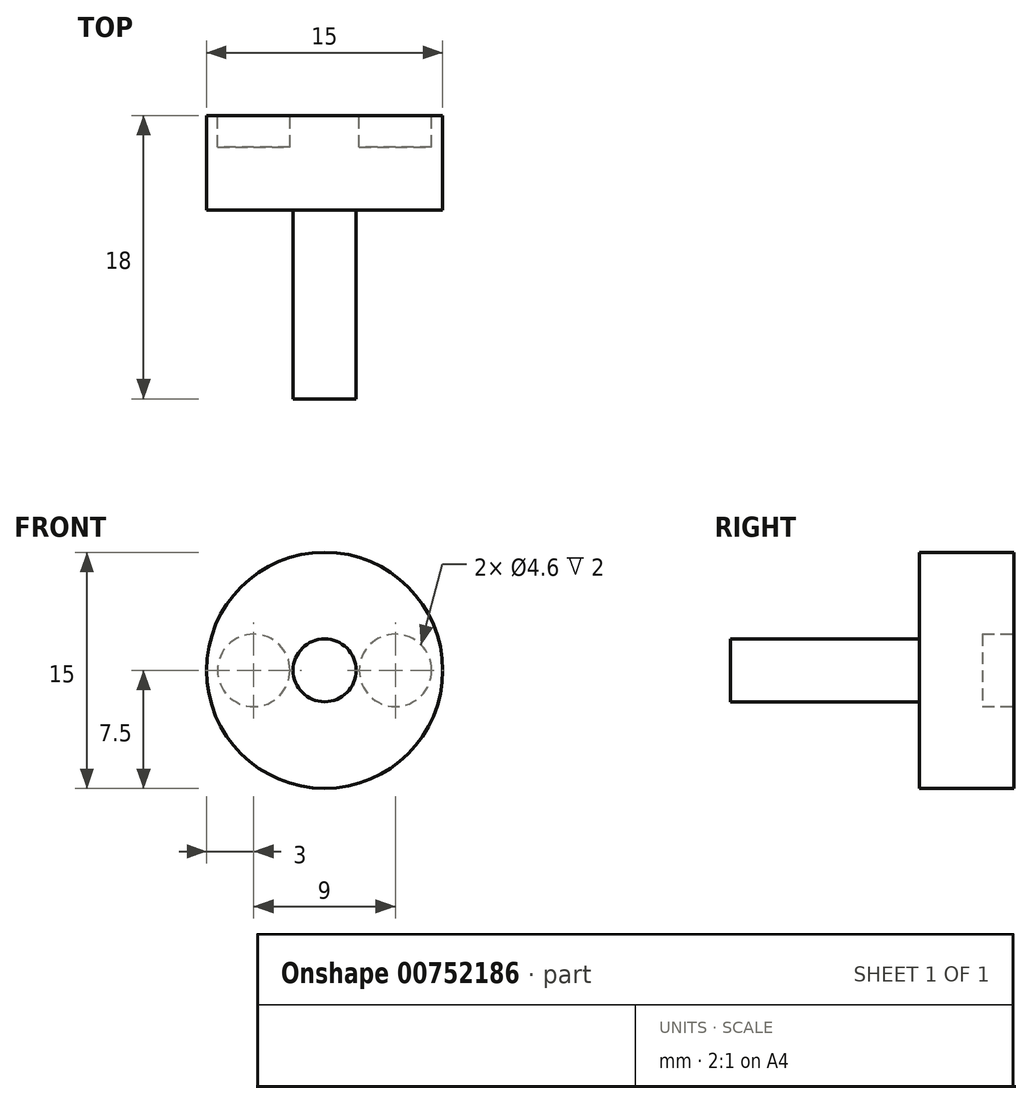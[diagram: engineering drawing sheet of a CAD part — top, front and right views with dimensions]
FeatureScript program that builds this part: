
annotation { "Feature Type Name" : "Feature", "Feature Type Description" : "" }
export const myFeature = defineFeature(function(context is Context, id is Id, definition is map)
    precondition{}
    {
        {
            var Q0;
            Q0=qCreatedBy(makeId("Front.planeOp"),FACE);
            var sketch = newSketch(context, id + "F0", { "sketchPlane" : qUnion([Q0])});
            skCircle(sketch, "E0", {"center": v(0, 0) * mm, "radius": 7.5 * mm});
            skSolve(sketch);
        }
        {
            var Q0;
            Q0 = qSketchRegion(id + "F0", true);
            extrude(context, id + "F1", {"entities" : qUnion([Q0]), "depth" : 6 * mm, "offsetDistance" : 25 * mm});
        }
        {
            var Q0;
            Q0=makeQuery(id+"F1.opExtrude","CAP_FACE",FACE,{"disambiguationData":[OSD([sQuery(id+"F0.wireOp",EDGE,"E0")])],"isStart":false});
            var sketch = newSketch(context, id + "F2", { "sketchPlane" : qUnion([Q0])});
            skCircle(sketch, "E1", {"center": v(0, 0) * mm, "radius": 2 * mm});
            skSolve(sketch);
        }
        {
            var Q0;
            Q0 = qSketchRegion(id + "F2", true);
            extrude(context, id + "F3", {"entities" : qUnion([Q0]), "operationType" : NewBodyOperationType.ADD, "depth" : 12 * mm, "offsetDistance" : 25 * mm});
        }
        {
            var Q0;
            Q0=makeQuery(id+"F1.opExtrude","CAP_FACE",FACE,{"disambiguationData":[OSD([sQuery(id+"F0.wireOp",EDGE,"E0")])],"isStart":true});
            var sketch = newSketch(context, id + "F4", { "sketchPlane" : qUnion([Q0])});
            skCircle(sketch, "E2", {"center": v(-4.5, 0) * mm, "radius": 2.3 * mm});
            skCircle(sketch, "E3", {"center": v(4.5, 0) * mm, "radius": 2.3 * mm});
            skSolve(sketch);
        }
        {
            var Q0;
            Q0 = qSketchRegion(id + "F4", true);
            extrude(context, id + "F5", {"entities" : qUnion([Q0]), "operationType" : NewBodyOperationType.REMOVE, "flatOperationType" : FlatOperationType.REMOVE, "oppositeDirection" : true, "depth" : 2 * mm, "offsetDistance" : 25 * mm, "domain" : OperationDomain.MODEL});
        }
    });
